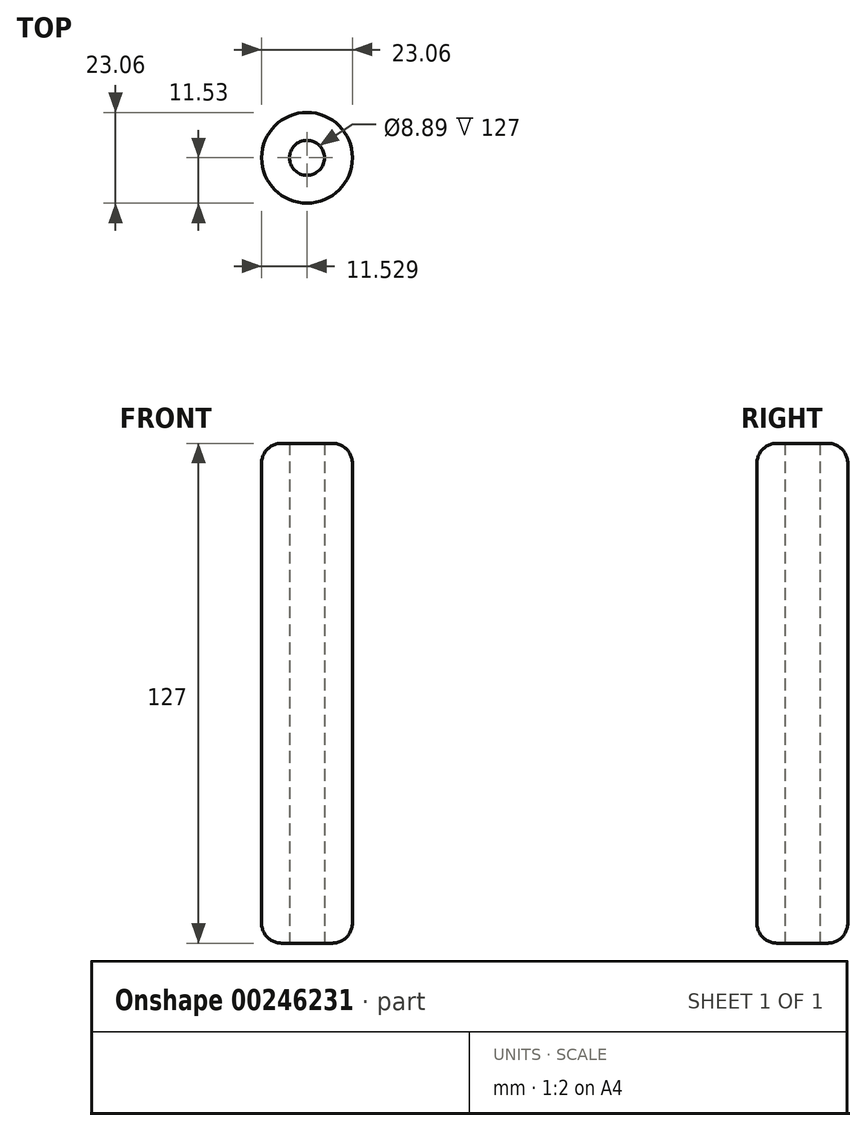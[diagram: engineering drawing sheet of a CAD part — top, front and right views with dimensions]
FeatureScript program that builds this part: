
annotation { "Feature Type Name" : "Feature", "Feature Type Description" : "" }
export const myFeature = defineFeature(function(context is Context, id is Id, definition is map)
    precondition{}
    {
        {
            var Q0;
            Q0=qCreatedBy(makeId("Top.planeOp"),FACE);
            var sketch = newSketch(context, id + "F0", { "sketchPlane" : qUnion([Q0])});
            skCircle(sketch, "E0", {"center": v(-11.53, 0) * mm, "radius": 11.53 * mm});
            skSolve(sketch);
        }
        {
            var Q0;
            Q0=makeQuery(id+"F0.imprint","IMPRINT",FACE,{"disambiguationData":[TD([[makeQuery(id+"F0.imprint","IMPRINT",EDGE,{"derivedFrom":sQuery(id+"F0.wireOp",EDGE,"E0")}),1.0]])]});
            extrude(context, id + "F1", {"entities" : qUnion([Q0]), "depth" : 127 * mm});
        }
        {
            var Q0;
            Q0=makeQuery(id+"F1.opExtrude","CAP_FACE",FACE,{"disambiguationData":[OSD([sQuery(id+"F0.wireOp",EDGE,"E0")])],"isStart":true});
            var sketch = newSketch(context, id + "F2", { "sketchPlane" : qUnion([Q0])});
            skCircle(sketch, "E1", {"center": v(-11.53, 0) * mm, "radius": 5.58 * mm});
            skSolve(sketch);
        }
        {
            var Q0;
            Q0=sQuery(id+"F2.wireOp",VERTEX,"E1.center");
            var Q1;
            Q1=makeQuery(id+"F1.opExtrude","SWEPT_BODY",BODY,{"disambiguationData":[OSD([sQuery(id+"F0.wireOp",EDGE,"E0")])]});
            hole(context, id + "F3", {"style" : HoleStyle.SIMPLE, "endStyle" : HoleEndStyle.THROUGH, "holeDiameter" : 8.9 * mm, "tappedDepth" : 12.7 * mm, "tapClearance" : 3, "locations" : qUnion([Q0]), "scope" : qUnion([Q1])});
        }
        {
            var Q0;
            Q0=makeQuery(id+"F1.opExtrude","CAP_EDGE",EDGE,{"disambiguationData":[OSD([sQuery(id+"F0.wireOp",EDGE,"E0")])],"isStart":false});
            fillet(context, id + "F4", {"entities" : qUnion([Q0]), "radius" : 5.08 * mm, "tangentPropagation" : true, "allowEdgeOverflow" : false});
        }
        {
            var Q0;
            Q0=makeQuery(id+"F1.opExtrude","CAP_EDGE",EDGE,{"disambiguationData":[OSD([sQuery(id+"F0.wireOp",EDGE,"E0")])],"isStart":true});
            fillet(context, id + "F5", {"entities" : qUnion([Q0]), "radius" : 5.08 * mm, "tangentPropagation" : true, "allowEdgeOverflow" : false});
        }
    });
